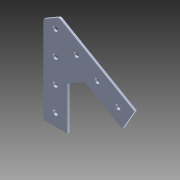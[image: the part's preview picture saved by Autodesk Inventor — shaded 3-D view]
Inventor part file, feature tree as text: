
AUTODESK INVENTOR PART (.ipt)
format: ipt  version: 2015 SP1 (Build 190203100, 203)  size: 229,888 bytes
history: native  units: in
note: dims shown in document units (in); Inventor stores cm internally (conversion verified against a paired STEP export)
features: extrude x5, sketch x5, projected_geometry x4, other x2, imported_body x1
ambient origin geometry x8: Origin, YZ Plane, XZ Plane, XY Plane, X Axis, Y Axis, Z Axis, Center Point
bodies: Body1 (feature_tree)
feature tree (17):
  other  "Cut-Extrude2"
  other  "Versaframe 60deg gusset1"
  extrude  "Extrusion3"  Depth=1.5in TaperAngle=0.0deg
  extrude  "Extrusion4"  Depth=0.09in
  extrude  "Extrusion5"  Depth=0.2in
  extrude  "Extrusion6"  Depth=0.2in
  extrude  "Extrusion7"  Depth=0.09in
  imported_body  "Base1"
  sketch  "Sketch3"  dims[d14=1.5in d15=0.0in d16=1.5in d17=0.0in]
  projected_geometry  "Projected Loop2"
  projected_geometry  "Projected Loop3"
  sketch  "Sketch4"  dims[d18=0.09in d19=0.0in d20=0.2in]
  projected_geometry  "Projected Loop4"
  projected_geometry  "Projected Loop5"
  sketch  "Sketch5"  dims[d21=0.2in d22=0.2in]
  sketch  "Sketch6"  dims[d23=0.2in d24=0.2in]
  sketch  "Sketch7"  dims[d25=0.2in d26=0.2in d27=0.5in d28=1.0in d29=0.5in d30=0.5in d31=0.09in d32=0.0in d33=0.09in d34=0.0in]
